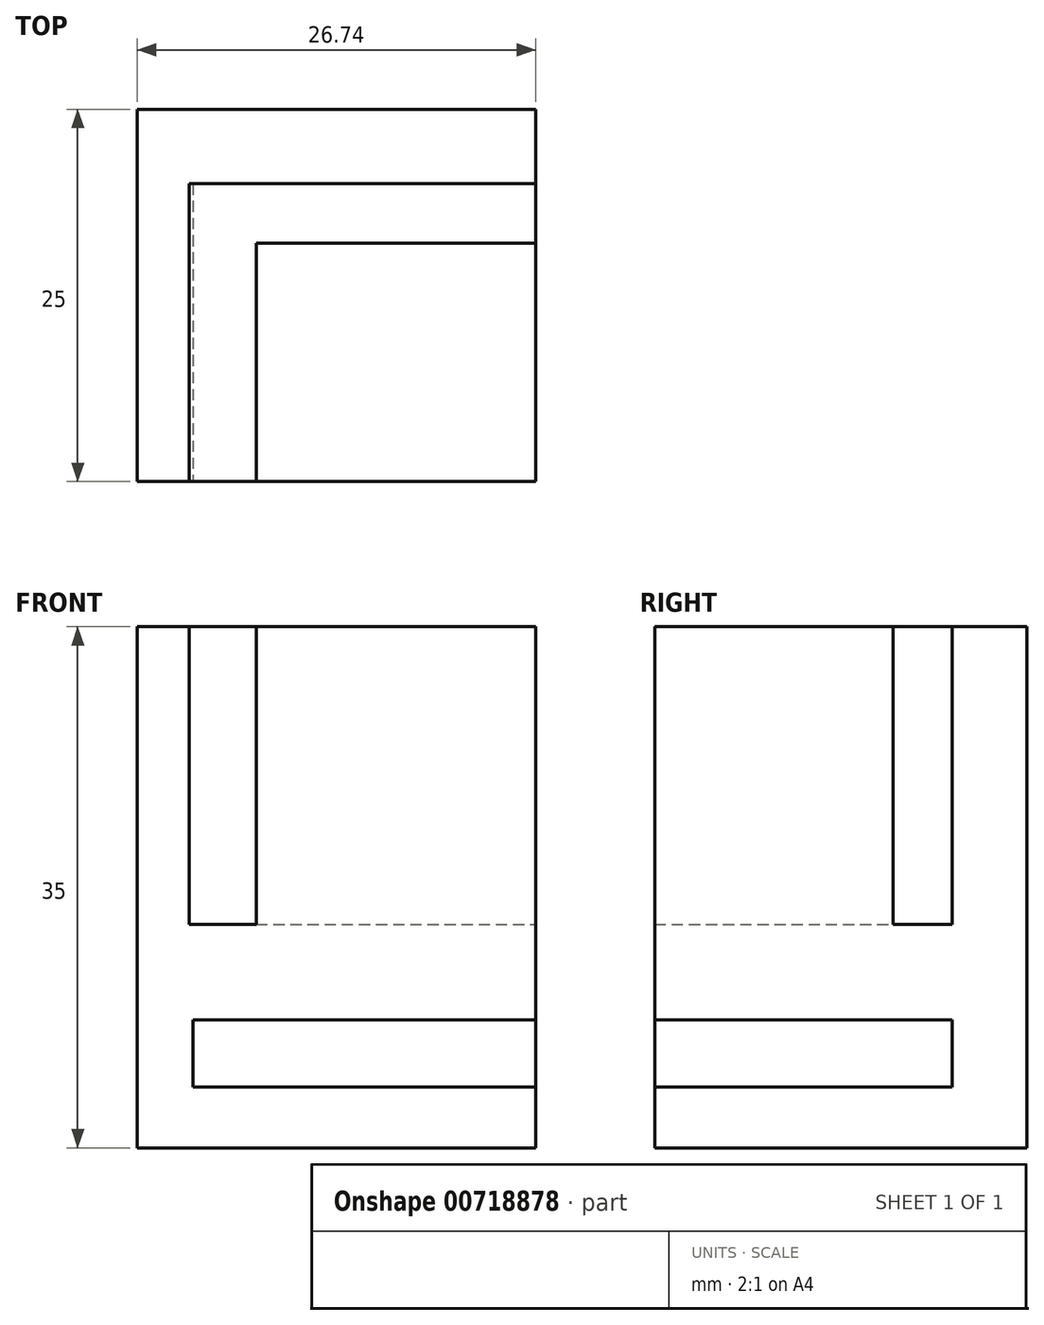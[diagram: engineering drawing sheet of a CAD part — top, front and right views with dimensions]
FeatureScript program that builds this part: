
annotation { "Feature Type Name" : "Feature", "Feature Type Description" : "" }
export const myFeature = defineFeature(function(context is Context, id is Id, definition is map)
    precondition{}
    {
        {
            var Q0;
            Q0=qCreatedBy(makeId("Top.planeOp"),FACE);
            var sketch = newSketch(context, id + "F0", { "sketchPlane" : qUnion([Q0])});
            skLineSegment(sketch, "E0.bottom", {"start": v(13.37, -12.5) * mm, "end": v(-13.37, -12.5) * mm});
            skLineSegment(sketch, "E0.top", {"start": v(13.37, 12.5) * mm, "end": v(-13.37, 12.5) * mm});
            skLineSegment(sketch, "E0.left", {"start": v(13.37, -12.5) * mm, "end": v(13.37, 12.5) * mm});
            skLineSegment(sketch, "E0.right", {"start": v(-13.37, -12.5) * mm, "end": v(-13.37, 12.5) * mm});
            skPoint(sketch, "E0.middle", {"position": v(0, 0) * mm});
            skSolve(sketch);
        }
        {
            var Q0;
            Q0 = qSketchRegion(id + "F0", true);
            extrude(context, id + "F1", {"entities" : qUnion([Q0]), "depth" : 35 * mm, "offsetDistance" : 25 * mm});
        }
        {
            var Q0;
            Q0=makeQuery(id+"F1.opExtrude","CAP_FACE",FACE,{"disambiguationData":[OSD([sQuery(id+"F0.wireOp",EDGE,"E0.bottom"),sQuery(id+"F0.wireOp",EDGE,"E0.top"),sQuery(id+"F0.wireOp",EDGE,"E0.left"),sQuery(id+"F0.wireOp",EDGE,"E0.right")])],"isStart":false});
            var sketch = newSketch(context, id + "F2", { "sketchPlane" : qUnion([Q0])});
            skLineSegment(sketch, "E1.bottom", {"start": v(-9.9, -12.5) * mm, "end": v(-5.4, -12.5) * mm});
            skLineSegment(sketch, "E1.top", {"start": v(-9.9, 7.5) * mm, "end": v(-5.4, 7.5) * mm});
            skLineSegment(sketch, "E1.left", {"start": v(-9.9, -12.5) * mm, "end": v(-9.9, 7.5) * mm});
            skLineSegment(sketch, "E1.right", {"start": v(-5.4, -12.5) * mm, "end": v(-5.4, 7.5) * mm});
            skSolve(sketch);
        }
        {
            var Q0;
            Q0 = qSketchRegion(id + "F2", true);
            extrude(context, id + "F3", {"entities" : qUnion([Q0]), "operationType" : NewBodyOperationType.REMOVE, "oppositeDirection" : true, "depth" : 20 * mm, "offsetDistance" : 25 * mm});
        }
        {
            var Q0;
            Q0=makeQuery(id+"F1.opExtrude","CAP_FACE",FACE,{"disambiguationData":[OSD([sQuery(id+"F0.wireOp",EDGE,"E0.bottom"),sQuery(id+"F0.wireOp",EDGE,"E0.top"),sQuery(id+"F0.wireOp",EDGE,"E0.left"),sQuery(id+"F0.wireOp",EDGE,"E0.right")])],"isStart":false});
            var sketch = newSketch(context, id + "F4", { "sketchPlane" : qUnion([Q0])});
            skLineSegment(sketch, "E2.bottom", {"start": v(-5.9, 7.5) * mm, "end": v(13.37, 7.5) * mm});
            skLineSegment(sketch, "E2.top", {"start": v(-5.9, 3.5) * mm, "end": v(13.37, 3.5) * mm});
            skLineSegment(sketch, "E2.left", {"start": v(-5.9, 7.5) * mm, "end": v(-5.9, 3.5) * mm});
            skLineSegment(sketch, "E2.right", {"start": v(13.37, 7.5) * mm, "end": v(13.37, 3.5) * mm});
            skSolve(sketch);
        }
        {
            var Q0;
            Q0 = qSketchRegion(id + "F4", true);
            extrude(context, id + "F5", {"entities" : qUnion([Q0]), "operationType" : NewBodyOperationType.REMOVE, "oppositeDirection" : true, "depth" : 20 * mm, "offsetDistance" : 25 * mm});
        }
        {
            var Q0;
            Q0=makeQuery(id+"F1.opExtrude","SWEPT_FACE",FACE,{"disambiguationData":[OSD([sQuery(id+"F0.wireOp",EDGE,"E0.bottom")])]});
            var sketch = newSketch(context, id + "F6", { "sketchPlane" : qUnion([Q0])});
            skLineSegment(sketch, "E3.bottom", {"start": v(13.37, 4.09) * mm, "end": v(-9.63, 4.09) * mm});
            skLineSegment(sketch, "E3.top", {"start": v(13.37, 8.59) * mm, "end": v(-9.63, 8.59) * mm});
            skLineSegment(sketch, "E3.left", {"start": v(13.37, 4.09) * mm, "end": v(13.37, 8.59) * mm});
            skLineSegment(sketch, "E3.right", {"start": v(-9.63, 4.09) * mm, "end": v(-9.63, 8.59) * mm});
            skSolve(sketch);
        }
        {
            var Q0;
            Q0 = qSketchRegion(id + "F6", true);
            extrude(context, id + "F7", {"entities" : qUnion([Q0]), "operationType" : NewBodyOperationType.REMOVE, "oppositeDirection" : true, "depth" : 20 * mm, "offsetDistance" : 25 * mm});
        }
    });
